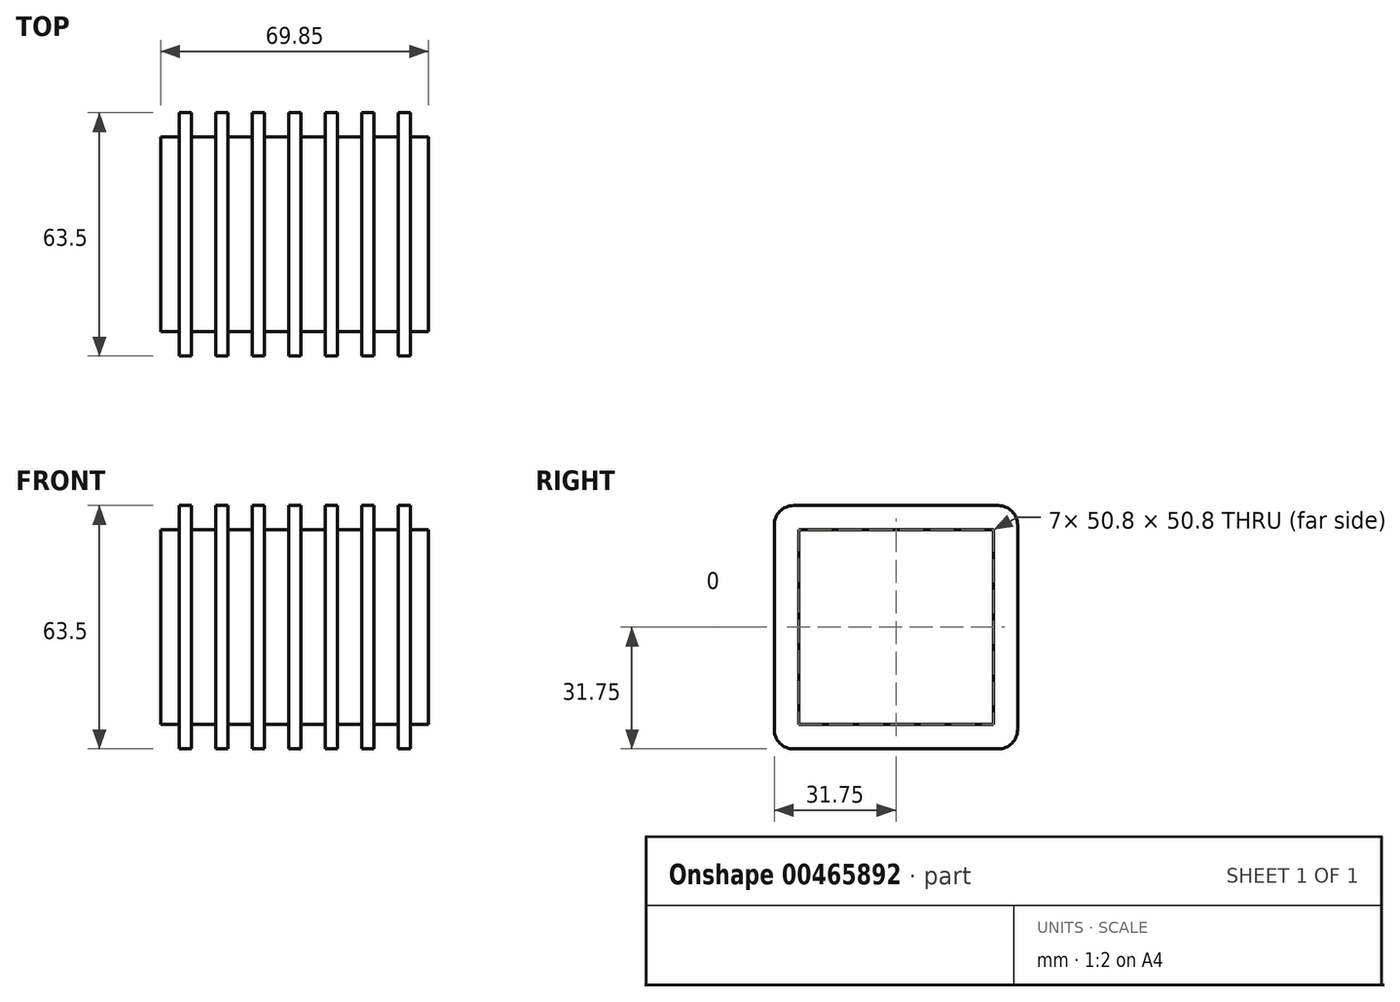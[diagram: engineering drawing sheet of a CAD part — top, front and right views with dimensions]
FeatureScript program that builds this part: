
annotation { "Feature Type Name" : "Feature", "Feature Type Description" : "" }
export const myFeature = defineFeature(function(context is Context, id is Id, definition is map)
    precondition{}
    {
        {
            var Q0;
            Q0=qCreatedBy(makeId("Front.planeOp"),FACE);
            var sketch = newSketch(context, id + "F0", { "sketchPlane" : qUnion([Q0])});
            skLineSegment(sketch, "E0.bottom", {"start": v(-63.5, 25.4) * mm, "end": v(63.5, 25.4) * mm});
            skLineSegment(sketch, "E0.top", {"start": v(-63.5, -25.4) * mm, "end": v(63.5, -25.4) * mm});
            skLineSegment(sketch, "E0.left", {"start": v(-63.5, 25.4) * mm, "end": v(-63.5, -25.4) * mm});
            skLineSegment(sketch, "E0.right", {"start": v(63.5, 25.4) * mm, "end": v(63.5, -25.4) * mm});
            skPoint(sketch, "E0.middle", {"position": v(0, 0) * mm});
            skSolve(sketch);
        }
        {
            var Q0;
            Q0=makeQuery(id+"F0.imprint","IMPRINT",FACE,{"disambiguationData":[TD([[makeQuery(id+"F0.imprint","IMPRINT",EDGE,{"derivedFrom":sQuery(id+"F0.wireOp",EDGE,"E0.bottom")}),-1.0]])]});
            extrude(context, id + "F1", {"entities" : qUnion([Q0]), "endBound" : BoundingType.SYMMETRIC, "depth" : 50.8 * mm, "offsetDistance" : 25.4 * mm});
        }
        {
            var Q0;
            Q0=qCreatedBy(makeId("Front.planeOp"),FACE);
            var sketch = newSketch(context, id + "F2", { "sketchPlane" : qUnion([Q0])});
            skPoint(sketch, "E1.middle", {"position": v(0, 0) * mm});
            skLineSegment(sketch, "E2.bottom", {"start": v(-1.59, 31.75) * mm, "end": v(1.59, 31.75) * mm});
            skLineSegment(sketch, "E2.top", {"start": v(-1.59, -31.75) * mm, "end": v(1.59, -31.75) * mm});
            skLineSegment(sketch, "E2.left", {"start": v(-1.59, 31.75) * mm, "end": v(-1.59, -31.75) * mm});
            skLineSegment(sketch, "E2.right", {"start": v(1.59, 31.75) * mm, "end": v(1.59, -31.75) * mm});
            skLineSegment(sketch, "E3", {"start": v(0, 0) * mm, "end": v(9.53, 0) * mm});
            skLineSegment(sketch, "E4", {"start": v(9.53, 0) * mm, "end": v(19.05, 0) * mm});
            skLineSegment(sketch, "E5", {"start": v(19.05, 0) * mm, "end": v(28.58, 0) * mm});
            skLineSegment(sketch, "E6", {"start": v(28.58, 0) * mm, "end": v(38.1, 0) * mm});
            skLineSegment(sketch, "E7", {"start": v(38.1, 0) * mm, "end": v(47.62, 0) * mm});
            skLineSegment(sketch, "E8", {"start": v(47.62, 0) * mm, "end": v(57.15, 0) * mm});
            skLineSegment(sketch, "E9.bottom", {"start": v(7.94, 31.75) * mm, "end": v(11.11, 31.75) * mm});
            skLineSegment(sketch, "E9.top", {"start": v(7.94, -31.75) * mm, "end": v(11.11, -31.75) * mm});
            skLineSegment(sketch, "E9.left", {"start": v(7.94, 31.75) * mm, "end": v(7.94, -31.75) * mm});
            skLineSegment(sketch, "E9.right", {"start": v(11.11, 31.75) * mm, "end": v(11.11, -31.75) * mm});
            skPoint(sketch, "E9.middle", {"position": v(9.53, 0) * mm});
            skLineSegment(sketch, "E10.bottom", {"start": v(17.46, 31.75) * mm, "end": v(20.64, 31.75) * mm});
            skLineSegment(sketch, "E10.top", {"start": v(17.46, -31.75) * mm, "end": v(20.64, -31.75) * mm});
            skLineSegment(sketch, "E10.left", {"start": v(17.46, 31.75) * mm, "end": v(17.46, -31.75) * mm});
            skLineSegment(sketch, "E10.right", {"start": v(20.64, 31.75) * mm, "end": v(20.64, -31.75) * mm});
            skPoint(sketch, "E10.middle", {"position": v(19.05, 0) * mm});
            skLineSegment(sketch, "E11.bottom", {"start": v(26.99, 31.75) * mm, "end": v(30.16, 31.75) * mm});
            skLineSegment(sketch, "E11.top", {"start": v(26.99, -31.75) * mm, "end": v(30.16, -31.75) * mm});
            skLineSegment(sketch, "E11.left", {"start": v(26.99, 31.75) * mm, "end": v(26.99, -31.75) * mm});
            skLineSegment(sketch, "E11.right", {"start": v(30.16, 31.75) * mm, "end": v(30.16, -31.75) * mm});
            skPoint(sketch, "E11.middle", {"position": v(28.58, 0) * mm});
            skLineSegment(sketch, "E12.bottom", {"start": v(36.51, 31.75) * mm, "end": v(39.69, 31.75) * mm});
            skLineSegment(sketch, "E12.top", {"start": v(36.51, -31.75) * mm, "end": v(39.69, -31.75) * mm});
            skLineSegment(sketch, "E12.left", {"start": v(36.51, 31.75) * mm, "end": v(36.51, -31.75) * mm});
            skLineSegment(sketch, "E12.right", {"start": v(39.69, 31.75) * mm, "end": v(39.69, -31.75) * mm});
            skPoint(sketch, "E12.middle", {"position": v(38.1, 0) * mm});
            skLineSegment(sketch, "E13.bottom", {"start": v(46.04, 31.75) * mm, "end": v(49.21, 31.75) * mm});
            skLineSegment(sketch, "E13.top", {"start": v(46.04, -31.75) * mm, "end": v(49.21, -31.75) * mm});
            skLineSegment(sketch, "E13.left", {"start": v(46.04, 31.75) * mm, "end": v(46.04, -31.75) * mm});
            skLineSegment(sketch, "E13.right", {"start": v(49.21, 31.75) * mm, "end": v(49.21, -31.75) * mm});
            skPoint(sketch, "E13.middle", {"position": v(47.62, 0) * mm});
            skLineSegment(sketch, "E14.bottom", {"start": v(55.56, 31.75) * mm, "end": v(58.74, 31.75) * mm});
            skLineSegment(sketch, "E14.top", {"start": v(55.56, -31.75) * mm, "end": v(58.74, -31.75) * mm});
            skLineSegment(sketch, "E14.left", {"start": v(55.56, 31.75) * mm, "end": v(55.56, -31.75) * mm});
            skLineSegment(sketch, "E14.right", {"start": v(58.74, 31.75) * mm, "end": v(58.74, -31.75) * mm});
            skPoint(sketch, "E14.middle", {"position": v(57.15, 0) * mm});
            skSolve(sketch);
        }
        {
            var Q0;
            {var subQ3=sQuery(id+"F2.wireOp",EDGE,"E14.bottom");Q0=makeQuery(id+"F2.imprint","IMPRINT",FACE,{"disambiguationData":[TD([[makeQuery(id+"F2.imprint","IMPRINT",EDGE,{"derivedFrom":subQ3}),-1.0]])]});}
            var Q1;
            {var subQ1=sQuery(id+"F2.wireOp",EDGE,"E13.bottom");Q1=makeQuery(id+"F2.imprint","IMPRINT",FACE,{"disambiguationData":[TD([[makeQuery(id+"F2.imprint","IMPRINT",EDGE,{"derivedFrom":subQ1}),-1.0]])]});}
            var Q2;
            {var subQ1=sQuery(id+"F2.wireOp",EDGE,"E12.bottom");Q2=makeQuery(id+"F2.imprint","IMPRINT",FACE,{"disambiguationData":[TD([[makeQuery(id+"F2.imprint","IMPRINT",EDGE,{"derivedFrom":subQ1}),-1.0]])]});}
            var Q3;
            {var subQ0=sQuery(id+"F2.wireOp",EDGE,"E11.bottom");Q3=makeQuery(id+"F2.imprint","IMPRINT",FACE,{"disambiguationData":[TD([[makeQuery(id+"F2.imprint","IMPRINT",EDGE,{"derivedFrom":subQ0}),-1.0]])]});}
            var Q4;
            {var subQ0=sQuery(id+"F2.wireOp",EDGE,"E10.bottom");Q4=makeQuery(id+"F2.imprint","IMPRINT",FACE,{"disambiguationData":[TD([[makeQuery(id+"F2.imprint","IMPRINT",EDGE,{"derivedFrom":subQ0}),-1.0]])]});}
            var Q5;
            {var subQ1=sQuery(id+"F2.wireOp",EDGE,"E9.bottom");Q5=makeQuery(id+"F2.imprint","IMPRINT",FACE,{"disambiguationData":[TD([[makeQuery(id+"F2.imprint","IMPRINT",EDGE,{"derivedFrom":subQ1}),-1.0]])]});}
            var Q6;
            {var subQ1=sQuery(id+"F2.wireOp",EDGE,"E2.bottom");Q6=makeQuery(id+"F2.imprint","IMPRINT",FACE,{"disambiguationData":[TD([[makeQuery(id+"F2.imprint","IMPRINT",EDGE,{"derivedFrom":subQ1}),-1.0]])]});}
            var Q7;
            {var subQ1=sQuery(id+"F2.wireOp",EDGE,"E9.top");Q7=makeQuery(id+"F2.imprint","IMPRINT",FACE,{"disambiguationData":[TD([[makeQuery(id+"F2.imprint","IMPRINT",EDGE,{"derivedFrom":subQ1}),1.0]])]});}
            var Q8;
            {var subQ1=sQuery(id+"F2.wireOp",EDGE,"E10.top");Q8=makeQuery(id+"F2.imprint","IMPRINT",FACE,{"disambiguationData":[TD([[makeQuery(id+"F2.imprint","IMPRINT",EDGE,{"derivedFrom":subQ1}),1.0]])]});}
            var Q9;
            {var subQ0=sQuery(id+"F2.wireOp",EDGE,"E11.top");Q9=makeQuery(id+"F2.imprint","IMPRINT",FACE,{"disambiguationData":[TD([[makeQuery(id+"F2.imprint","IMPRINT",EDGE,{"derivedFrom":subQ0}),1.0]])]});}
            var Q10;
            {var subQ0=sQuery(id+"F2.wireOp",EDGE,"E12.top");Q10=makeQuery(id+"F2.imprint","IMPRINT",FACE,{"disambiguationData":[TD([[makeQuery(id+"F2.imprint","IMPRINT",EDGE,{"derivedFrom":subQ0}),1.0]])]});}
            var Q11;
            {var subQ1=sQuery(id+"F2.wireOp",EDGE,"E13.top");Q11=makeQuery(id+"F2.imprint","IMPRINT",FACE,{"disambiguationData":[TD([[makeQuery(id+"F2.imprint","IMPRINT",EDGE,{"derivedFrom":subQ1}),1.0]])]});}
            extrude(context, id + "F3", {"entities" : qUnion([Q0, Q1, Q2, Q3, Q4, Q5, Q6, Q7, Q8, Q9, Q10, Q11]), "operationType" : NewBodyOperationType.ADD, "endBound" : BoundingType.SYMMETRIC, "depth" : 63.5 * mm, "offsetDistance" : 25.4 * mm});
        }
        {
            var Q0;
            Q0=makeQuery(id+"F3.opExtrude","CAP_EDGE",EDGE,{"disambiguationData":[OSD([sQuery(id+"F2.wireOp",EDGE,"E2.bottom")])],"isStart":false});
            var Q1;
            Q1=makeQuery(id+"F3.opExtrude","CAP_EDGE",EDGE,{"disambiguationData":[OSD([sQuery(id+"F2.wireOp",EDGE,"E9.bottom")])],"isStart":false});
            var Q2;
            Q2=makeQuery(id+"F3.opExtrude","CAP_EDGE",EDGE,{"disambiguationData":[OSD([sQuery(id+"F2.wireOp",EDGE,"E10.bottom")])],"isStart":false});
            var Q3;
            Q3=makeQuery(id+"F3.opExtrude","CAP_EDGE",EDGE,{"disambiguationData":[OSD([sQuery(id+"F2.wireOp",EDGE,"E11.bottom")])],"isStart":false});
            var Q4;
            Q4=makeQuery(id+"F3.opExtrude","CAP_EDGE",EDGE,{"disambiguationData":[OSD([sQuery(id+"F2.wireOp",EDGE,"E12.bottom")])],"isStart":false});
            var Q5;
            Q5=makeQuery(id+"F3.opExtrude","CAP_EDGE",EDGE,{"disambiguationData":[OSD([sQuery(id+"F2.wireOp",EDGE,"E13.bottom")])],"isStart":false});
            var Q6;
            Q6=makeQuery(id+"F3.opExtrude","CAP_EDGE",EDGE,{"disambiguationData":[OSD([sQuery(id+"F2.wireOp",EDGE,"E14.bottom")])],"isStart":false});
            fillet(context, id + "F4", {"entities" : qUnion([Q0, Q1, Q2, Q3, Q4, Q5, Q6]), "radius" : 5.08 * mm, "tangentPropagation" : true, "allowEdgeOverflow" : false});
        }
        {
            var Q0;
            Q0=makeQuery(id+"F3.opExtrude","CAP_EDGE",EDGE,{"disambiguationData":[OSD([sQuery(id+"F2.wireOp",EDGE,"E2.bottom")])],"isStart":true});
            var Q1;
            Q1=makeQuery(id+"F3.opExtrude","CAP_EDGE",EDGE,{"disambiguationData":[OSD([sQuery(id+"F2.wireOp",EDGE,"E9.bottom")])],"isStart":true});
            var Q2;
            Q2=makeQuery(id+"F3.opExtrude","CAP_EDGE",EDGE,{"disambiguationData":[OSD([sQuery(id+"F2.wireOp",EDGE,"E10.bottom")])],"isStart":true});
            var Q3;
            Q3=makeQuery(id+"F3.opExtrude","CAP_EDGE",EDGE,{"disambiguationData":[OSD([sQuery(id+"F2.wireOp",EDGE,"E11.bottom")])],"isStart":true});
            var Q4;
            Q4=makeQuery(id+"F3.opExtrude","CAP_EDGE",EDGE,{"disambiguationData":[OSD([sQuery(id+"F2.wireOp",EDGE,"E12.bottom")])],"isStart":true});
            var Q5;
            Q5=makeQuery(id+"F3.opExtrude","CAP_EDGE",EDGE,{"disambiguationData":[OSD([sQuery(id+"F2.wireOp",EDGE,"E13.bottom")])],"isStart":true});
            var Q6;
            Q6=makeQuery(id+"F3.opExtrude","CAP_EDGE",EDGE,{"disambiguationData":[OSD([sQuery(id+"F2.wireOp",EDGE,"E14.bottom")])],"isStart":true});
            fillet(context, id + "F5", {"entities" : qUnion([Q0, Q1, Q2, Q3, Q4, Q5, Q6]), "radius" : 5.08 * mm, "tangentPropagation" : true, "allowEdgeOverflow" : false});
        }
        {
            var Q0;
            Q0=makeQuery(id+"F3.opExtrude","CAP_EDGE",EDGE,{"disambiguationData":[OSD([sQuery(id+"F2.wireOp",EDGE,"E14.top")])],"isStart":true});
            var Q1;
            Q1=makeQuery(id+"F3.opExtrude","CAP_EDGE",EDGE,{"disambiguationData":[OSD([sQuery(id+"F2.wireOp",EDGE,"E13.top")])],"isStart":true});
            var Q2;
            Q2=makeQuery(id+"F3.opExtrude","CAP_EDGE",EDGE,{"disambiguationData":[OSD([sQuery(id+"F2.wireOp",EDGE,"E12.top")])],"isStart":true});
            var Q3;
            Q3=makeQuery(id+"F3.opExtrude","CAP_EDGE",EDGE,{"disambiguationData":[OSD([sQuery(id+"F2.wireOp",EDGE,"E10.top")])],"isStart":true});
            var Q4;
            Q4=makeQuery(id+"F3.opExtrude","CAP_EDGE",EDGE,{"disambiguationData":[OSD([sQuery(id+"F2.wireOp",EDGE,"E11.top")])],"isStart":true});
            var Q5;
            Q5=makeQuery(id+"F3.opExtrude","CAP_EDGE",EDGE,{"disambiguationData":[OSD([sQuery(id+"F2.wireOp",EDGE,"E9.top")])],"isStart":true});
            var Q6;
            Q6=makeQuery(id+"F3.opExtrude","CAP_EDGE",EDGE,{"disambiguationData":[OSD([sQuery(id+"F2.wireOp",EDGE,"E2.top")])],"isStart":true});
            fillet(context, id + "F6", {"entities" : qUnion([Q0, Q1, Q2, Q3, Q4, Q5, Q6]), "radius" : 5.08 * mm, "tangentPropagation" : true, "allowEdgeOverflow" : false});
        }
        {
            var Q0;
            Q0=makeQuery(id+"F3.opExtrude","CAP_EDGE",EDGE,{"disambiguationData":[OSD([sQuery(id+"F2.wireOp",EDGE,"E9.top")])],"isStart":false});
            var Q1;
            Q1=makeQuery(id+"F3.opExtrude","CAP_EDGE",EDGE,{"disambiguationData":[OSD([sQuery(id+"F2.wireOp",EDGE,"E10.top")])],"isStart":false});
            var Q2;
            Q2=makeQuery(id+"F3.opExtrude","CAP_EDGE",EDGE,{"disambiguationData":[OSD([sQuery(id+"F2.wireOp",EDGE,"E11.top")])],"isStart":false});
            var Q3;
            Q3=makeQuery(id+"F3.opExtrude","CAP_EDGE",EDGE,{"disambiguationData":[OSD([sQuery(id+"F2.wireOp",EDGE,"E12.top")])],"isStart":false});
            var Q4;
            Q4=makeQuery(id+"F3.opExtrude","CAP_EDGE",EDGE,{"disambiguationData":[OSD([sQuery(id+"F2.wireOp",EDGE,"E13.top")])],"isStart":false});
            var Q5;
            Q5=makeQuery(id+"F3.opExtrude","CAP_EDGE",EDGE,{"disambiguationData":[OSD([sQuery(id+"F2.wireOp",EDGE,"E14.top")])],"isStart":false});
            fillet(context, id + "F7", {"entities" : qUnion([Q0, Q1, Q2, Q3, Q4, Q5]), "radius" : 5.08 * mm, "tangentPropagation" : true, "allowEdgeOverflow" : false});
        }
        {
            var Q0;
            Q0=qCreatedBy(makeId("Top.planeOp"),FACE);
            var sketch = newSketch(context, id + "F8", { "sketchPlane" : qUnion([Q0])});
            skLineSegment(sketch, "E15", {"start": v(0, 0) * mm, "end": v(-63.5, 0) * mm});
            skLineSegment(sketch, "E16", {"start": v(-63.5, 0) * mm, "end": v(-63.5, 25.4) * mm});
            skLineSegment(sketch, "E17", {"start": v(-63.5, 25.4) * mm, "end": v(-6.35, 25.4) * mm});
            skLineSegment(sketch, "E18", {"start": v(-6.35, 25.4) * mm, "end": v(-6.35, -25.4) * mm});
            skLineSegment(sketch, "E19", {"start": v(-6.35, -25.4) * mm, "end": v(-63.5, -25.4) * mm});
            skSolve(sketch);
        }
        {
            var Q0;
            {var subQ1=sQuery(id+"F0.wireOp",EDGE,"E0.left");var subQ3=sQuery(id+"F0.wireOp",EDGE,"E0.bottom");Q0=makeQuery(id+"F3.boolean.opBoolean","SPLIT",FACE,{"disambiguationData":[TD([makeQuery(id+"F1.opExtrude","SWEPT_FACE",FACE,{"disambiguationData":[OSD([subQ1])]})])],"derivedFrom":makeQuery(id+"F1.opExtrude","SWEPT_FACE",FACE,{"disambiguationData":[OSD([subQ3])]})});}
            extrude(context, id + "F9", {"entities" : qUnion([Q0]), "operationType" : NewBodyOperationType.REMOVE, "oppositeDirection" : true, "depth" : 25.4 * mm, "offsetDistance" : 25.4 * mm});
        }
        {
            var Q0;
            {var subQ0=sQuery(id+"F8.wireOp",EDGE,"E16");Q0=makeQuery(id+"F8.imprint","IMPRINT",FACE,{"disambiguationData":[TD([[makeQuery(id+"F8.imprint","IMPRINT",EDGE,{"derivedFrom":subQ0}),-1.0]])]});}
            extrude(context, id + "F10", {"entities" : qUnion([Q0]), "operationType" : NewBodyOperationType.REMOVE, "oppositeDirection" : true, "depth" : 25.4 * mm, "offsetDistance" : 25.4 * mm});
        }
        {
            var Q0;
            Q0=qCreatedBy(makeId("Top.planeOp"),FACE);
            var sketch = newSketch(context, id + "F11", { "sketchPlane" : qUnion([Q0])});
            skLineSegment(sketch, "E20", {"start": v(0, 0) * mm, "end": v(-6.35, 0) * mm});
            skLineSegment(sketch, "E21", {"start": v(-6.35, 0) * mm, "end": v(-6.35, -25.4) * mm});
            skLineSegment(sketch, "E22", {"start": v(-6.35, -25.4) * mm, "end": v(-63.5, -25.4) * mm});
            skLineSegment(sketch, "E23", {"start": v(-63.5, -25.4) * mm, "end": v(-63.5, 0) * mm});
            skLineSegment(sketch, "E24", {"start": v(-63.5, 0) * mm, "end": v(-6.35, 0) * mm});
            skSolve(sketch);
        }
        {
            var Q0;
            Q0=makeQuery(id+"F11.imprint","IMPRINT",FACE,{"disambiguationData":[TD([[makeQuery(id+"F11.imprint","IMPRINT",EDGE,{"derivedFrom":sQuery(id+"F11.wireOp",EDGE,"E21")}),-1.0]])]});
            extrude(context, id + "F12", {"entities" : qUnion([Q0]), "operationType" : NewBodyOperationType.REMOVE, "oppositeDirection" : true, "depth" : 25.4 * mm, "offsetDistance" : 25.4 * mm});
        }
        {
            var Q0;
            Q0=makeQuery(id+"F9.boolean.opBoolean","COPY",FACE,{"derivedFrom":makeQuery(id+"F9.opExtrude","CAP_FACE",FACE,{"disambiguationData":[OSD([sQuery(id+"F0.wireOp",EDGE,"E0.bottom")])],"isStart":false})});
            extrude(context, id + "F13", {"entities" : qUnion([Q0]), "operationType" : NewBodyOperationType.ADD, "depth" : 25.4 * mm, "offsetDistance" : 25.4 * mm});
        }
        {
            var Q0;
            Q0=makeQuery(id+"F3.opExtrude","CAP_EDGE",EDGE,{"disambiguationData":[OSD([sQuery(id+"F2.wireOp",EDGE,"E2.top")])],"isStart":false});
            fillet(context, id + "F14", {"entities" : qUnion([Q0]), "radius" : 5.08 * mm, "tangentPropagation" : true, "allowEdgeOverflow" : false});
        }
    });
